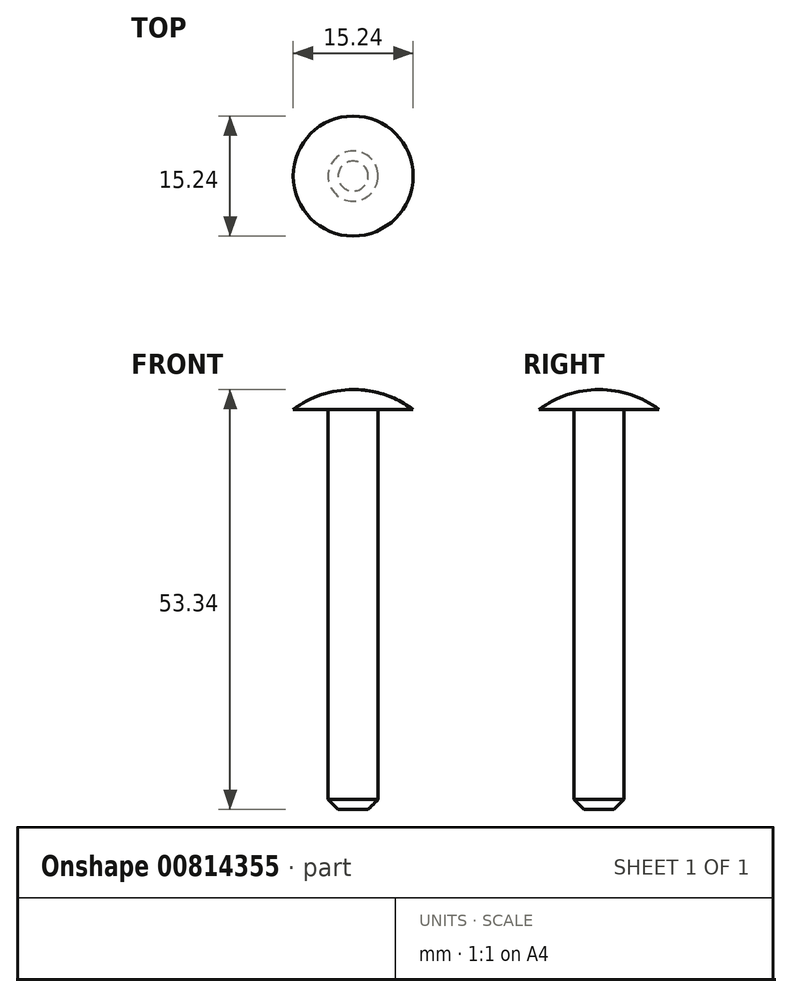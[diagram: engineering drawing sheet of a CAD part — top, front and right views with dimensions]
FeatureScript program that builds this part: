
annotation { "Feature Type Name" : "Feature", "Feature Type Description" : "" }
export const myFeature = defineFeature(function(context is Context, id is Id, definition is map)
    precondition{}
    {
        {
            var Q0;
            Q0=qCreatedBy(makeId("Front.planeOp"),FACE);
            var sketch = newSketch(context, id + "F0", { "sketchPlane" : qUnion([Q0])});
            skLineSegment(sketch, "E0", {"start": v(0, 42.6) * mm, "end": v(0, -55.7) * mm, "construction": true});
            skLineSegment(sketch, "E1", {"start": v(0, -50.8) * mm, "end": v(3.18, -50.8) * mm});
            skLineSegment(sketch, "E2", {"start": v(3.18, -50.8) * mm, "end": v(3.18, 0) * mm});
            skLineSegment(sketch, "E3", {"start": v(3.18, 0) * mm, "end": v(7.62, 0) * mm});
            skCircle(sketch, "E4", {"center": v(0, -10.16) * mm, "radius": 12.7 * mm});
            skLineSegment(sketch, "E5", {"start": v(0, -50.8) * mm, "end": v(0, 2.54) * mm});
            skSolve(sketch);
        }
        {
            var Q0;
            {var subQ5=sQuery(id+"F0.wireOp",EDGE,"E3");Q0=makeQuery(id+"F0.imprint","IMPRINT",FACE,{"disambiguationData":[TD([[makeQuery(id+"F0.imprint","IMPRINT",EDGE,{"derivedFrom":subQ5}),1.0]])]});}
            var Q1;
            {var subQ0=sQuery(id+"F0.wireOp",EDGE,"E1");Q1=makeQuery(id+"F0.imprint","IMPRINT",FACE,{"disambiguationData":[TD([[makeQuery(id+"F0.imprint","IMPRINT",EDGE,{"derivedFrom":subQ0}),1.0]])]});}
            var Q2;
            Q2=sQuery(id+"F0.wireOp",EDGE,"E0");
            revolve(context, id + "F1", {"surfaceOperationType" : NewSurfaceOperationType.NEW, "entities" : qUnion([Q0, Q1]), "axis" : qUnion([Q2]), "revolveType" : RevolveType.FULL});
        }
        {
            var Q0;
            Q0=makeQuery(id+"F1.opRevolve","SWEPT_EDGE",EDGE,{"disambiguationData":[OSD([sQuery(id+"F0.wireOp",EDGE,"E1"),sQuery(id+"F0.wireOp",EDGE,"E2")])]});
            chamfer(context, id + "F2", {"entities" : qUnion([Q0]), "width" : 1.27 * mm, "tangentPropagation" : true});
        }
    });
